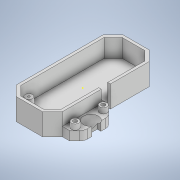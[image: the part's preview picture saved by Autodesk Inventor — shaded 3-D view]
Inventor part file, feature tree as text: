
AUTODESK INVENTOR PART (.ipt)
format: ipt  version: 2020 (Build 240168000, 168)  size: 316,416 bytes
history: native  units: mm
features: sketch x15, extrude x12, projected_geometry x2, plane x1, revolve x1, chamfer x1, fillet x1
ambient origin geometry x8: Origin, YZ Plane, XZ Plane, XY Plane, X Axis, Y Axis, Z Axis, Center Point
bodies: Volumenkörper1 (feature_tree)
feature tree (33):
  extrude  "Extrusion1"  Depth=21.5mm
  extrude  "Extrusion2"  Depth=5.5mm
  extrude  "Extrusion3"  Depth=5.5mm
  extrude  "Extrusion7"  Depth=5.5mm
  extrude  "Extrusion8"  Depth=5.5mm
  extrude  "Extrusion15"  Depth=2.0mm
  extrude  "Extrusion16"  Depth=5.5mm
  plane  "Arbeitsebene1"
  revolve  "Umdrehung1"
  extrude  "Extrusion17"  Depth=5.5mm
  extrude  "Extrusion18"  Depth=5.5mm
  extrude  "Extrusion19"  Depth=5.5mm
  extrude  "Extrusion20"  Depth=2.0mm TaperAngle=0.0deg
  sketch  "Skizze24"  dims[d26=2.0mm]
  extrude  "Extrusion21"  Depth=2.0mm
  sketch  "Skizze26"  dims[d28=4.0mm d29=4.0mm d30=1.1mm d31=1.1mm d32=5.0mm d33=0.0mm d44=5.0mm d45=8.0mm d46=0.0mm d47=12.0mm d48=0.0mm d74=0.5mm d75=0.5mm d80=5.0mm d81=5.0mm d82=5.0mm d83=5.0mm d84=5.0mm d85=5.0mm d86=5.0mm d87=5.0mm d88=10.0mm d89=0.0mm d90=10.0mm d91=0.0mm d92=-6.0mm d93=8.5mm d94=90.0deg d95=7.0mm d96=0.0mm d97=5.0mm d98=4.0mm d99=0.0mm d100=2.0mm d101=0.0mm d102=4.0mm d103=3.0mm d104=4.0mm d105=3.0mm d106=2.1mm d107=2.1mm d108=0.0mm d109=0.0mm d110=4.0mm d111=4.0mm d112=3.0mm d113=0.0mm d114=4.0mm d115=2.0mm d116=45.0deg d117=4.0mm]
  chamfer  "Fase2"  Distance=4.0mm
  fillet  "Rundung2"  Radius=1.1mm
  sketch  "Skizze1"  dims[d0=21.5mm d1=55.0mm]
  sketch  "Skizze3"  dims[d2=5.5mm d3=5.5mm]
  projected_geometry  "Projizierte Kontur1"
  sketch  "Skizze4"  dims[d4=5.5mm d5=5.5mm]
  sketch  "Skizze8"  dims[d6=5.5mm d7=5.5mm]
  sketch  "Skizze9"  dims[d8=5.5mm d9=5.5mm]
  sketch  "Skizze17"  dims[d10=2.0mm d11=2.0mm]
  sketch  "Skizze18"  dims[d12=5.5mm d13=5.5mm]
  projected_geometry  "Projizierte Kontur5"
  sketch  "Skizze19"  dims[d14=5.5mm d15=5.5mm]
  sketch  "Skizze20"  dims[d16=5.5mm d17=5.5mm]
  sketch  "Skizze21"  dims[d18=5.5mm d19=5.5mm]
  sketch  "Skizze22"  dims[d20=10.0mm d21=0.0mm d22=2.0mm d23=0.0mm]
  sketch  "Skizze23"  dims[d24=2.0mm d25=21.0mm]
  sketch  "Skizze25"  dims[d27=18.3mm]
